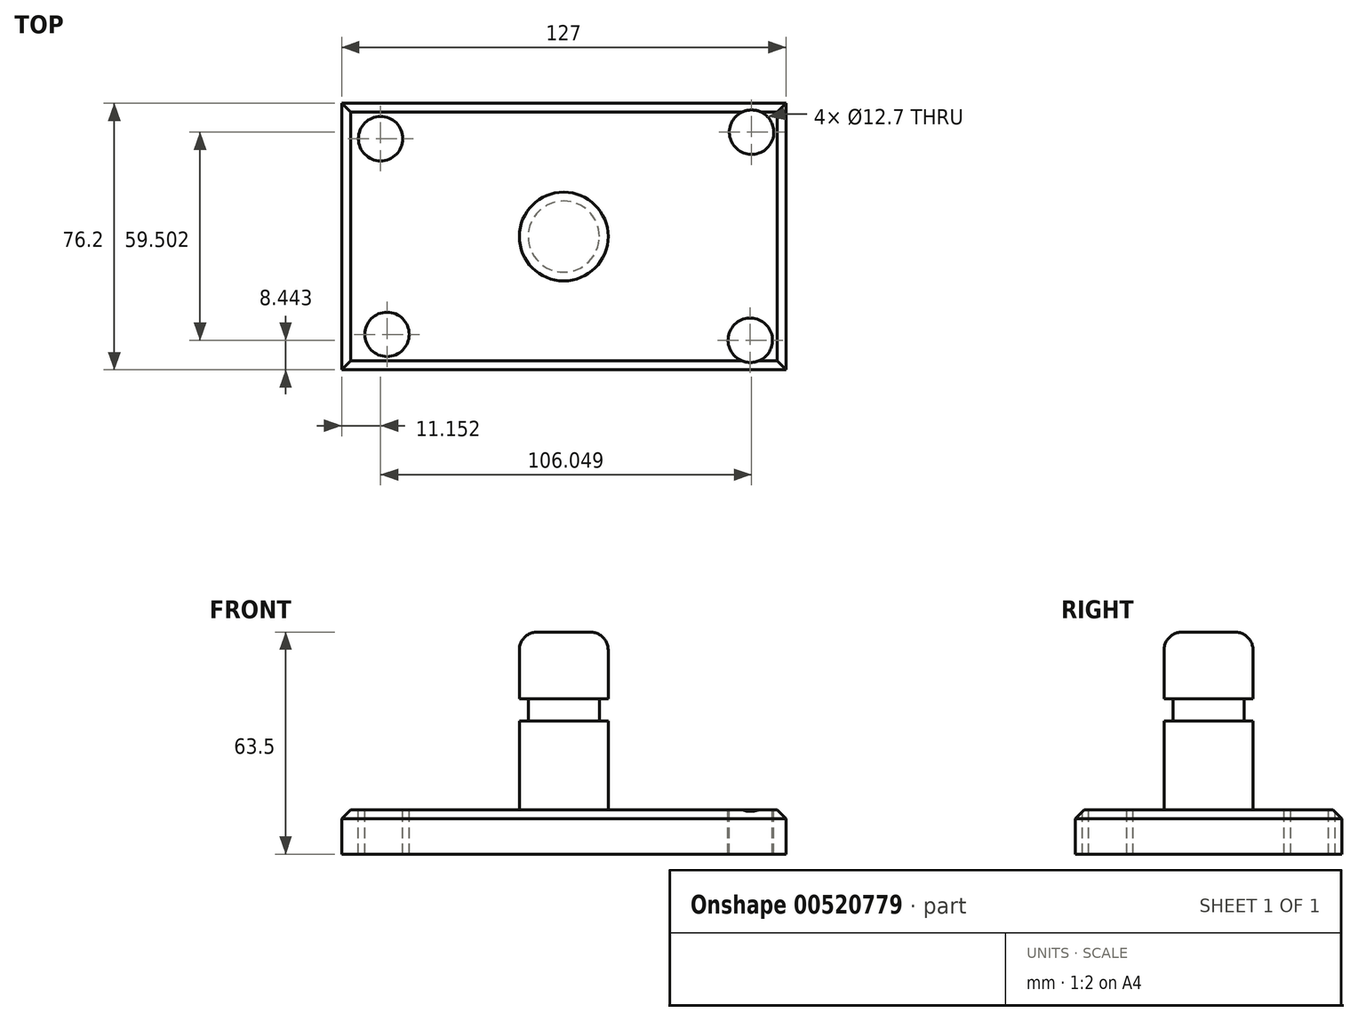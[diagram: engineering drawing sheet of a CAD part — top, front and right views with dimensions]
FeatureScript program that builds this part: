
annotation { "Feature Type Name" : "Feature", "Feature Type Description" : "" }
export const myFeature = defineFeature(function(context is Context, id is Id, definition is map)
    precondition{}
    {
        {
            var Q0;
            Q0=qCreatedBy(makeId("Top.planeOp"),FACE);
            var sketch = newSketch(context, id + "F0", { "sketchPlane" : qUnion([Q0])});
            skLineSegment(sketch, "E0.bottom", {"start": v(63.5, 38.1) * mm, "end": v(-63.5, 38.1) * mm});
            skLineSegment(sketch, "E0.top", {"start": v(63.5, -38.1) * mm, "end": v(-63.5, -38.1) * mm});
            skLineSegment(sketch, "E0.left", {"start": v(63.5, 38.1) * mm, "end": v(63.5, -38.1) * mm});
            skLineSegment(sketch, "E0.right", {"start": v(-63.5, 38.1) * mm, "end": v(-63.5, -38.1) * mm});
            skPoint(sketch, "E0.middle", {"position": v(0, 0) * mm});
            skSolve(sketch);
        }
        {
            var Q0;
            Q0=makeQuery(id+"F0.imprint","IMPRINT",FACE,{"disambiguationData":[TD([[makeQuery(id+"F0.imprint","IMPRINT",EDGE,{"derivedFrom":sQuery(id+"F0.wireOp",EDGE,"E0.bottom")}),1.0]])]});
            extrude(context, id + "F1", {"entities" : qUnion([Q0]), "depth" : 12.7 * mm, "offsetDistance" : 25.4 * mm});
        }
        {
            var Q0;
            Q0=makeQuery(id+"F1.opExtrude","CAP_FACE",FACE,{"disambiguationData":[OSD([sQuery(id+"F0.wireOp",EDGE,"E0.bottom"),sQuery(id+"F0.wireOp",EDGE,"E0.top"),sQuery(id+"F0.wireOp",EDGE,"E0.left"),sQuery(id+"F0.wireOp",EDGE,"E0.right")])],"isStart":false});
            var sketch = newSketch(context, id + "F2", { "sketchPlane" : qUnion([Q0])});
            skCircle(sketch, "E1", {"center": v(-52.35, 28) * mm, "radius": 6.35 * mm});
            skCircle(sketch, "E2", {"center": v(53.7, 29.84) * mm, "radius": 6.35 * mm});
            skCircle(sketch, "E3", {"center": v(-50.52, -27.97) * mm, "radius": 6.35 * mm});
            skCircle(sketch, "E4", {"center": v(53.33, -29.66) * mm, "radius": 6.35 * mm});
            skSolve(sketch);
        }
        {
            var Q0;
            Q0 = qSketchRegion(id + "F2", true);
            extrude(context, id + "F3", {"entities" : qUnion([Q0]), "operationType" : NewBodyOperationType.REMOVE, "endBound" : BoundingType.THROUGH_ALL, "oppositeDirection" : true, "depth" : 25.4 * mm, "offsetDistance" : 25.4 * mm});
        }
        {
            var Q0;
            Q0=qCreatedBy(makeId("Front.planeOp"),FACE);
            var sketch = newSketch(context, id + "F4", { "sketchPlane" : qUnion([Q0])});
            skLineSegment(sketch, "E5.bottom", {"start": v(0, 12.7) * mm, "end": v(12.7, 12.7) * mm});
            skLineSegment(sketch, "E5.top", {"start": v(0, 63.5) * mm, "end": v(12.7, 63.5) * mm});
            skLineSegment(sketch, "E5.left", {"start": v(0, 12.7) * mm, "end": v(0, 63.5) * mm});
            skLineSegment(sketch, "E5.right", {"start": v(12.7, 12.7) * mm, "end": v(12.7, 63.5) * mm});
            skSolve(sketch);
        }
        {
            var Q0;
            Q0 = qSketchRegion(id + "F4", true);
            var Q1;
            Q1=sQuery(id+"F4.wireOp",EDGE,"E5.left");
            revolve(context, id + "F5", {"operationType" : NewBodyOperationType.ADD, "entities" : qUnion([Q0]), "axis" : qUnion([Q1]), "revolveType" : RevolveType.FULL});
        }
        {
            var Q0;
            Q0=qCreatedBy(makeId("Front.planeOp"),FACE);
            var sketch = newSketch(context, id + "F6", { "sketchPlane" : qUnion([Q0])});
            skLineSegment(sketch, "E6.bottom", {"start": v(10.16, 44.45) * mm, "end": v(23.18, 44.45) * mm});
            skLineSegment(sketch, "E6.top", {"start": v(10.16, 38.1) * mm, "end": v(23.18, 38.1) * mm});
            skLineSegment(sketch, "E6.left", {"start": v(10.16, 44.45) * mm, "end": v(10.16, 38.1) * mm});
            skLineSegment(sketch, "E6.right", {"start": v(23.18, 44.45) * mm, "end": v(23.18, 38.1) * mm});
            skSolve(sketch);
        }
        {
            var Q0;
            Q0=makeQuery(id+"F6.imprint","IMPRINT",FACE,{"disambiguationData":[TD([[makeQuery(id+"F6.imprint","IMPRINT",EDGE,{"derivedFrom":sQuery(id+"F6.wireOp",EDGE,"E6.bottom")}),-1.0]])]});
            var Q1;
            Q1=sQuery(id+"F4.wireOp",EDGE,"E5.left");
            revolve(context, id + "F7", {"operationType" : NewBodyOperationType.REMOVE, "entities" : qUnion([Q0]), "axis" : qUnion([Q1]), "revolveType" : RevolveType.FULL, "oppositeDirection" : true});
        }
        {
            var Q0;
            Q0=makeQuery(id+"F5.opRevolve","SWEPT_FACE",FACE,{"disambiguationData":[OSD([sQuery(id+"F4.wireOp",EDGE,"E5.top")])]});
            var Q1;
            Q1=makeQuery(id+"F5.opRevolve","SWEPT_EDGE",EDGE,{"disambiguationData":[OSD([sQuery(id+"F4.wireOp",EDGE,"E5.bottom"),sQuery(id+"F4.wireOp",EDGE,"E5.right")])]});
            fillet(context, id + "F8", {"entities" : qUnion([Q0, Q1]), "radius" : 5.08 * mm, "tangentPropagation" : true, "allowEdgeOverflow" : false});
        }
        {
            var Q0;
            Q0=makeQuery(id+"F1.opExtrude","CAP_EDGE",EDGE,{"disambiguationData":[OSD([sQuery(id+"F0.wireOp",EDGE,"E0.top")])],"isStart":false});
            var Q1;
            Q1=makeQuery(id+"F1.opExtrude","CAP_EDGE",EDGE,{"disambiguationData":[OSD([sQuery(id+"F0.wireOp",EDGE,"E0.left")])],"isStart":false});
            var Q2;
            Q2=makeQuery(id+"F1.opExtrude","CAP_EDGE",EDGE,{"disambiguationData":[OSD([sQuery(id+"F0.wireOp",EDGE,"E0.bottom")])],"isStart":false});
            var Q3;
            Q3=makeQuery(id+"F1.opExtrude","CAP_EDGE",EDGE,{"disambiguationData":[OSD([sQuery(id+"F0.wireOp",EDGE,"E0.right")])],"isStart":false});
            chamfer(context, id + "F9", {"entities" : qUnion([Q0, Q1, Q2, Q3]), "width" : 2.54 * mm, "tangentPropagation" : true});
        }
    });
